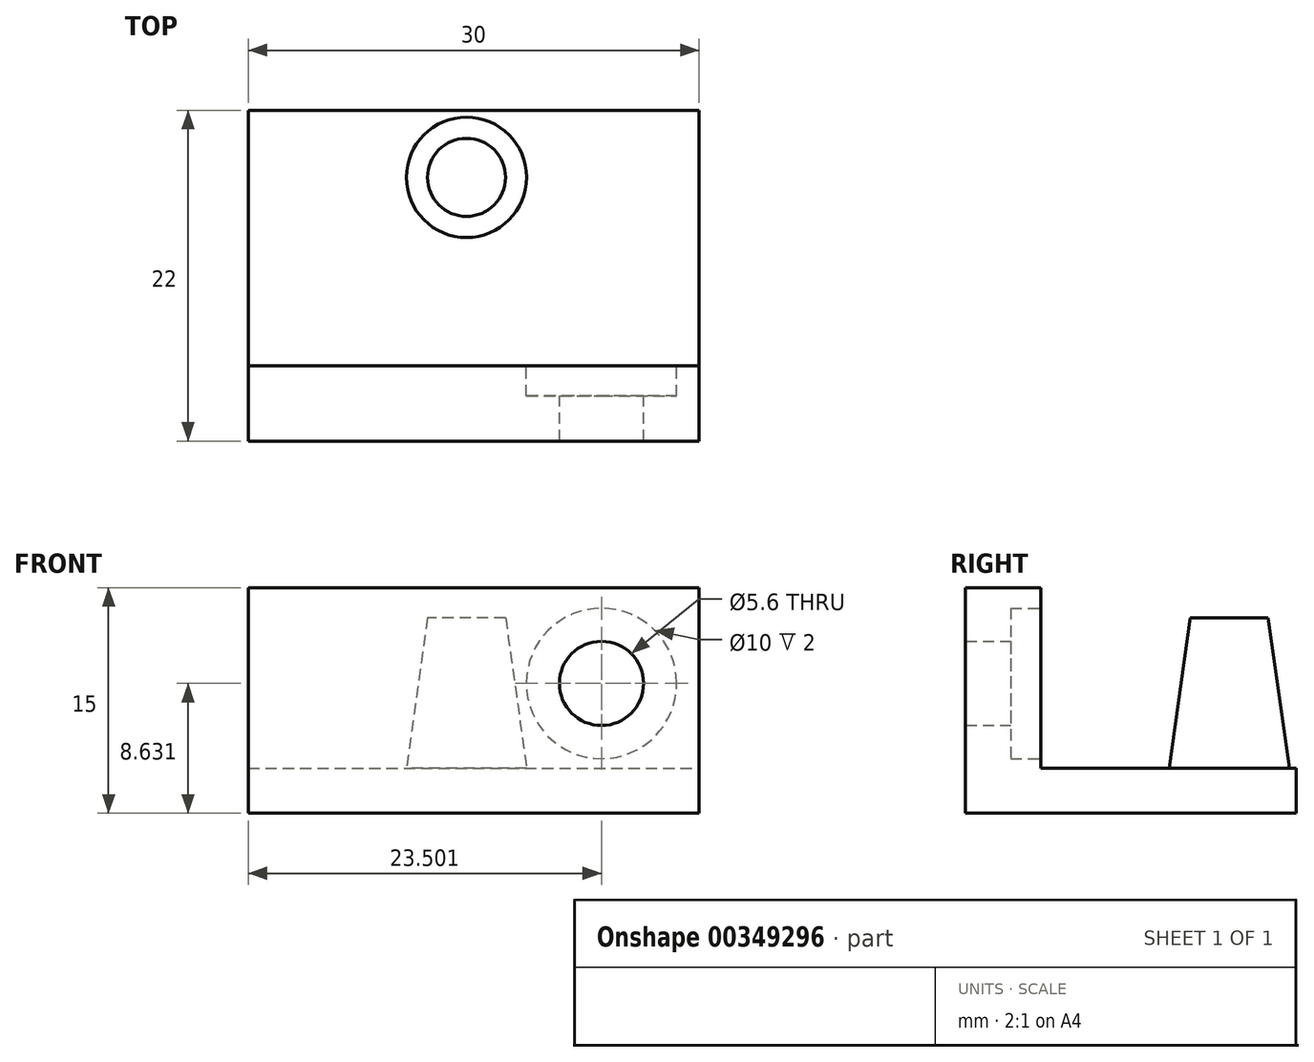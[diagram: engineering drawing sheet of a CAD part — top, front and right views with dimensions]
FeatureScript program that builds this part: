
annotation { "Feature Type Name" : "Feature", "Feature Type Description" : "" }
export const myFeature = defineFeature(function(context is Context, id is Id, definition is map)
    precondition{}
    {
        {
            var Q0;
            Q0=qCreatedBy(makeId("Top.planeOp"),FACE);
            var sketch = newSketch(context, id + "F0", { "sketchPlane" : qUnion([Q0])});
            skLineSegment(sketch, "E0.bottom", {"start": v(-14.52, 0) * mm, "end": v(15.48, 0) * mm});
            skLineSegment(sketch, "E0.top", {"start": v(-14.52, 22) * mm, "end": v(15.48, 22) * mm});
            skLineSegment(sketch, "E0.left", {"start": v(-14.52, 0) * mm, "end": v(-14.52, 22) * mm});
            skLineSegment(sketch, "E0.right", {"start": v(15.48, 0) * mm, "end": v(15.48, 22) * mm});
            skSolve(sketch);
        }
        {
            var Q0;
            Q0 = qSketchRegion(id + "F0", true);
            extrude(context, id + "F1", {"entities" : qUnion([Q0]), "depth" : 3 * mm, "offsetDistance" : 25 * mm});
        }
        {
            var Q0;
            Q0=makeQuery(id+"F1.opExtrude","CAP_FACE",FACE,{"disambiguationData":[OSD([sQuery(id+"F0.wireOp",EDGE,"E0.bottom"),sQuery(id+"F0.wireOp",EDGE,"E0.top"),sQuery(id+"F0.wireOp",EDGE,"E0.left"),sQuery(id+"F0.wireOp",EDGE,"E0.right")])],"isStart":false});
            var sketch = newSketch(context, id + "F2", { "sketchPlane" : qUnion([Q0])});
            skLineSegment(sketch, "E1.bottom", {"start": v(-14.52, 0) * mm, "end": v(15.48, 0) * mm});
            skLineSegment(sketch, "E1.top", {"start": v(-14.52, 5) * mm, "end": v(15.48, 5) * mm});
            skLineSegment(sketch, "E1.left", {"start": v(-14.52, 0) * mm, "end": v(-14.52, 5) * mm});
            skLineSegment(sketch, "E1.right", {"start": v(15.48, 0) * mm, "end": v(15.48, 5) * mm});
            skCircle(sketch, "E2", {"center": v(0, 17.54) * mm, "radius": 4 * mm});
            skSolve(sketch);
        }
        {
            var Q0;
            {var subQ0=sQuery(id+"F2.wireOp",EDGE,"E2");var subQ1=makeQuery(id+"F1.opExtrude","CAP_EDGE",EDGE,{"disambiguationData":[OSD([sQuery(id+"F0.wireOp",EDGE,"E0.top")])],"isStart":false});var subQ2=makeQuery(id+"F2.imprint","INTERSECT",VERTEX,{"disambiguationData":[OD(0.0)],"derivedFrom":[subQ1,subQ0]});Q0=makeQuery(id+"F2.imprint","IMPRINT",FACE,{"disambiguationData":[TD([[makeQuery(id+"F2.imprint","IMPRINT",EDGE,{"disambiguationData":[TD([[subQ2,-1.0]])],"derivedFrom":subQ0}),1.0]])]});}
            extrude(context, id + "F3", {"entities" : qUnion([Q0]), "operationType" : NewBodyOperationType.ADD, "depth" : 10 * mm, "offsetDistance" : 25 * mm, "hasDraft" : true, "draftAngle" : 8 * degree, "draftPullDirection" : true});
        }
        {
            var Q0;
            Q0=makeQuery(id+"F2.imprint","IMPRINT",FACE,{"disambiguationData":[TD([[makeQuery(id+"F2.imprint","IMPRINT",EDGE,{"derivedFrom":sQuery(id+"F2.wireOp",EDGE,"E1.bottom")}),1.0]])]});
            extrude(context, id + "F4", {"entities" : qUnion([Q0]), "operationType" : NewBodyOperationType.ADD, "depth" : 12 * mm, "offsetDistance" : 25 * mm});
        }
        {
            var Q0;
            Q0=makeQuery(id+"F4.opExtrude","SWEPT_FACE",FACE,{"disambiguationData":[OSD([sQuery(id+"F2.wireOp",EDGE,"E1.top")])]});
            var sketch = newSketch(context, id + "F5", { "sketchPlane" : qUnion([Q0])});
            skPoint(sketch, "E3", {"position": v(-8.98, 8.63) * mm});
            skSolve(sketch);
        }
        {
            var Q0;
            Q0=sQuery(id+"F5.wireOp",VERTEX,"E3");
            var Q1;
            Q1=makeQuery(id+"F1.opExtrude","SWEPT_BODY",BODY,{"disambiguationData":[OSD([sQuery(id+"F0.wireOp",EDGE,"E0.bottom"),sQuery(id+"F0.wireOp",EDGE,"E0.top"),sQuery(id+"F0.wireOp",EDGE,"E0.left"),sQuery(id+"F0.wireOp",EDGE,"E0.right")])]});
            hole(context, id + "F6", {"style" : HoleStyle.C_BORE, "endStyle" : HoleEndStyle.BLIND, "holeDiameter" : 5.6 * mm, "cBoreDiameter" : 10 * mm, "cBoreDepth" : 2 * mm, "holeDepth" : 15 * mm, "isTappedThrough" : true, "tappedDepth" : 12 * mm, "tapClearance" : 3, "startFromSketch" : true, "locations" : qUnion([Q0]), "scope" : qUnion([Q1])});
        }
    });
